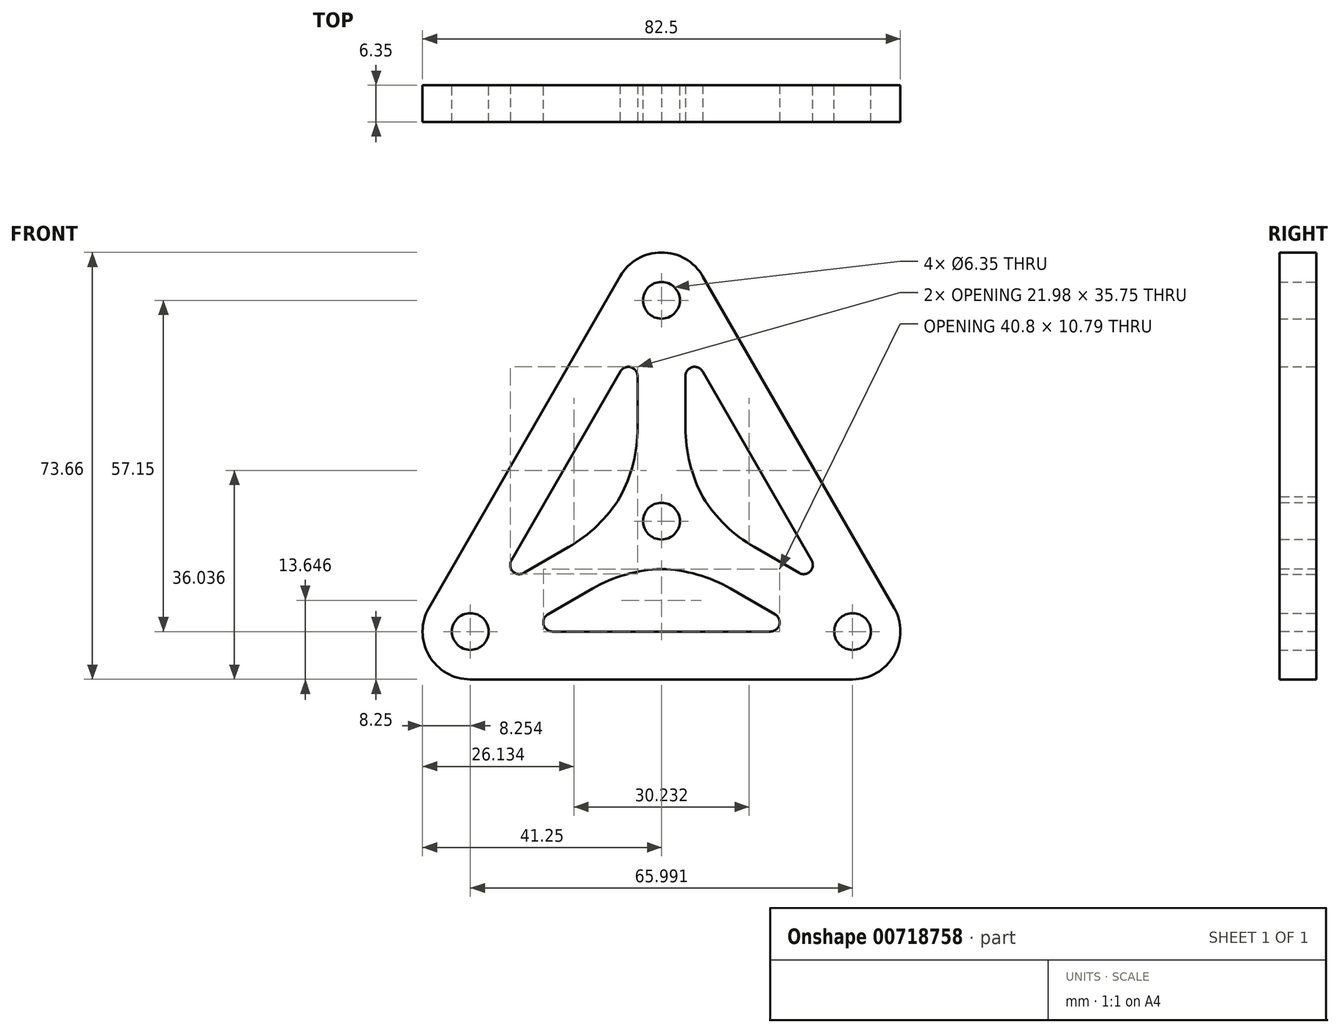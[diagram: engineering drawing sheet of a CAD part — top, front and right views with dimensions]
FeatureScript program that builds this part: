
annotation { "Feature Type Name" : "Feature", "Feature Type Description" : "" }
export const myFeature = defineFeature(function(context is Context, id is Id, definition is map)
    precondition{}
    {
        {
            var Q0;
            Q0=qCreatedBy(makeId("Front.planeOp"),FACE);
            var sketch = newSketch(context, id + "F0", { "sketchPlane" : qUnion([Q0])});
            skPoint(sketch, "E0", {"position": v(0, 38.1) * mm});
            skCircle(sketch, "E1", {"center": v(0, 38.1) * mm, "radius": 3.18 * mm});
            skCircle(sketch, "E2.1.0", {"center": v(-33, -19.05) * mm, "radius": 3.18 * mm});
            skPoint(sketch, "E2.1.1", {"position": v(-33, -19.05) * mm});
            skCircle(sketch, "E2.2.0", {"center": v(33, -19.05) * mm, "radius": 3.18 * mm});
            skPoint(sketch, "E2.2.1", {"position": v(33, -19.05) * mm});
            skPoint(sketch, "E2.center", {"position": v(0, 0) * mm});
            skLineSegment(sketch, "E3", {"start": v(-33, -19.05) * mm, "end": v(0, 38.1) * mm, "construction": true});
            skLineSegment(sketch, "E4", {"start": v(33, -19.05) * mm, "end": v(-33, -19.05) * mm, "construction": true});
            skLineSegment(sketch, "E5", {"start": v(33, -19.05) * mm, "end": v(0, 38.1) * mm, "construction": true});
            skLineSegment(sketch, "E6.0", {"start": v(40.14, -14.92) * mm, "end": v(7.15, 42.23) * mm});
            skLineSegment(sketch, "E6.1", {"start": v(33, -27.3) * mm, "end": v(-33, -27.3) * mm});
            skLineSegment(sketch, "E6.2", {"start": v(-40.14, -14.92) * mm, "end": v(-7.15, 42.23) * mm});
            skPoint(sketch, "E7.visualSharp", {"position": v(0, 54.61) * mm});
            skArc(sketch, "E7.filletArc", {"start": v(7.15, 42.23) * mm, "mid": v(0, 46.36) * mm, "end": v(-7.15, 42.23) * mm});
            skPoint(sketch, "E8.visualSharp", {"position": v(47.3, -27.3) * mm});
            skArc(sketch, "E8.filletArc", {"start": v(33, -27.3) * mm, "mid": v(40.14, -23.18) * mm, "end": v(40.14, -14.92) * mm});
            skPoint(sketch, "E9.visualSharp", {"position": v(-47.3, -27.3) * mm});
            skArc(sketch, "E9.filletArc", {"start": v(-40.14, -14.92) * mm, "mid": v(-40.14, -23.18) * mm, "end": v(-33, -27.3) * mm});
            skSolve(sketch);
        }
        {
            var Q0;
            Q0=qSketchRegion(id+"F0",true);
            extrude(context, id + "F1", {"entities" : qUnion([Q0]), "depth" : 6.35 * mm, "offsetDistance" : 25.4 * mm});
        }
        {
            var Q0;
            Q0=makeQuery(id+"F1.opExtrude","CAP_FACE",FACE,{"disambiguationData":[OSD([sQuery(id+"F0.wireOp",EDGE,"E1"),sQuery(id+"F0.wireOp",EDGE,"E2.1.0"),sQuery(id+"F0.wireOp",EDGE,"E2.2.0"),sQuery(id+"F0.wireOp",EDGE,"E6.0"),sQuery(id+"F0.wireOp",EDGE,"E6.1"),sQuery(id+"F0.wireOp",EDGE,"E6.2"),sQuery(id+"F0.wireOp",EDGE,"E7.filletArc"),sQuery(id+"F0.wireOp",EDGE,"E8.filletArc"),sQuery(id+"F0.wireOp",EDGE,"E9.filletArc")])],"isStart":false});
            var sketch = newSketch(context, id + "F2", { "sketchPlane" : qUnion([Q0])});
            skCircle(sketch, "E10", {"center": v(0, 0) * mm, "radius": 3.18 * mm});
            skSolve(sketch);
        }
        {
            var Q0;
            Q0 = qSketchRegion(id + "F2", true);
            extrude(context, id + "F3", {"entities" : qUnion([Q0]), "operationType" : NewBodyOperationType.REMOVE, "endBound" : BoundingType.THROUGH_ALL, "oppositeDirection" : true, "depth" : 25.4 * mm, "offsetDistance" : 25.4 * mm});
        }
        {
            var Q0;
            Q0=makeQuery(id+"F1.opExtrude","CAP_FACE",FACE,{"disambiguationData":[OSD([sQuery(id+"F0.wireOp",EDGE,"E1"),sQuery(id+"F0.wireOp",EDGE,"E2.1.0"),sQuery(id+"F0.wireOp",EDGE,"E2.2.0"),sQuery(id+"F0.wireOp",EDGE,"E6.0"),sQuery(id+"F0.wireOp",EDGE,"E6.1"),sQuery(id+"F0.wireOp",EDGE,"E6.2"),sQuery(id+"F0.wireOp",EDGE,"E7.filletArc"),sQuery(id+"F0.wireOp",EDGE,"E8.filletArc"),sQuery(id+"F0.wireOp",EDGE,"E9.filletArc")])],"isStart":false});
            var sketch = newSketch(context, id + "F4", { "sketchPlane" : qUnion([Q0])});
            skCircle(sketch, "E11", {"center": v(-33, -19.05) * mm, "radius": 8.25 * mm, "construction": true});
            skCircle(sketch, "E12", {"center": v(0, 38.1) * mm, "radius": 8.26 * mm, "construction": true});
            skCircle(sketch, "E13", {"center": v(33, -19.05) * mm, "radius": 8.26 * mm, "construction": true});
            skCircle(sketch, "E14", {"center": v(0, 0) * mm, "radius": 8.26 * mm});
            skLineSegment(sketch, "E15", {"start": v(-28.87, -11.9) * mm, "end": v(-4.13, 30.95) * mm});
            skLineSegment(sketch, "E16.1.0", {"start": v(24.74, -19.05) * mm, "end": v(-24.74, -19.05) * mm});
            skLineSegment(sketch, "E16.2.0", {"start": v(4.13, 30.95) * mm, "end": v(28.87, -11.9) * mm});
            skLineSegment(sketch, "E17", {"start": v(-4.13, 30.95) * mm, "end": v(-4.13, 7.15) * mm});
            skLineSegment(sketch, "E18", {"start": v(0, 38.1) * mm, "end": v(0, 41.28) * mm, "construction": true});
            skLineSegment(sketch, "E19.MirrorCS", {"start": v(4.13, 30.95) * mm, "end": v(4.13, 7.15) * mm});
            skLineSegment(sketch, "E20.1.0", {"start": v(-28.87, -11.9) * mm, "end": v(-8.25, 0) * mm});
            skLineSegment(sketch, "E20.1.1", {"start": v(-24.74, -19.05) * mm, "end": v(-4.13, -7.15) * mm});
            skLineSegment(sketch, "E20.2.0", {"start": v(24.74, -19.05) * mm, "end": v(4.13, -7.15) * mm});
            skLineSegment(sketch, "E20.2.1", {"start": v(28.87, -11.9) * mm, "end": v(8.26, 0) * mm});
            skLineSegment(sketch, "E21", {"start": v(-4.13, 30.95) * mm, "end": v(-4.13, 30.95) * mm});
            skLineSegment(sketch, "E22", {"start": v(4.13, 30.95) * mm, "end": v(4.13, 30.95) * mm});
            skLineSegment(sketch, "E23.1.0", {"start": v(-28.87, -11.9) * mm, "end": v(-28.87, -11.9) * mm});
            skLineSegment(sketch, "E23.1.1", {"start": v(-24.74, -19.05) * mm, "end": v(-24.74, -19.05) * mm});
            skLineSegment(sketch, "E23.2.0", {"start": v(24.74, -19.05) * mm, "end": v(24.74, -19.05) * mm});
            skLineSegment(sketch, "E23.2.1", {"start": v(28.87, -11.9) * mm, "end": v(28.87, -11.9) * mm});
            skSolve(sketch);
        }
        {
            var Q0;
            {var subQ0=sQuery(id+"F4.wireOp",EDGE,"E15");Q0=makeQuery(id+"F4.imprint","IMPRINT",FACE,{"disambiguationData":[TD([[makeQuery(id+"F4.imprint","IMPRINT",EDGE,{"derivedFrom":subQ0}),-1.0]])]});}
            var Q1;
            {var subQ0=sQuery(id+"F4.wireOp",EDGE,"E16.1.0");Q1=makeQuery(id+"F4.imprint","IMPRINT",FACE,{"disambiguationData":[TD([[makeQuery(id+"F4.imprint","IMPRINT",EDGE,{"derivedFrom":subQ0}),-1.0]])]});}
            var Q2;
            {var subQ0=sQuery(id+"F4.wireOp",EDGE,"E16.2.0");Q2=makeQuery(id+"F4.imprint","IMPRINT",FACE,{"disambiguationData":[TD([[makeQuery(id+"F4.imprint","IMPRINT",EDGE,{"derivedFrom":subQ0}),-1.0]])]});}
            extrude(context, id + "F5", {"entities" : qUnion([Q0, Q1, Q2]), "operationType" : NewBodyOperationType.REMOVE, "endBound" : BoundingType.THROUGH_ALL, "oppositeDirection" : true, "depth" : 25.4 * mm, "offsetDistance" : 25.4 * mm});
        }
        {
            var Q0;
            Q0=makeQuery(id+"F5.boolean.opBoolean","COPY",EDGE,{"derivedFrom":makeQuery(id+"F5.opExtrude","SWEPT_EDGE",EDGE,{"disambiguationData":[OSD([sQuery(id+"F4.wireOp",EDGE,"E14"),sQuery(id+"F4.wireOp",EDGE,"E17")])]})});
            var Q1;
            Q1=makeQuery(id+"F5.boolean.opBoolean","COPY",EDGE,{"derivedFrom":makeQuery(id+"F5.opExtrude","SWEPT_EDGE",EDGE,{"disambiguationData":[OSD([sQuery(id+"F4.wireOp",EDGE,"E14"),sQuery(id+"F4.wireOp",EDGE,"E20.1.0")])]})});
            var Q2;
            Q2=makeQuery(id+"F5.boolean.opBoolean","COPY",EDGE,{"derivedFrom":makeQuery(id+"F5.opExtrude","SWEPT_EDGE",EDGE,{"disambiguationData":[OSD([sQuery(id+"F4.wireOp",EDGE,"E14"),sQuery(id+"F4.wireOp",EDGE,"E20.1.1")])]})});
            var Q3;
            Q3=makeQuery(id+"F5.boolean.opBoolean","COPY",EDGE,{"derivedFrom":makeQuery(id+"F5.opExtrude","SWEPT_EDGE",EDGE,{"disambiguationData":[OSD([sQuery(id+"F4.wireOp",EDGE,"E14"),sQuery(id+"F4.wireOp",EDGE,"E20.2.0")])]})});
            var Q4;
            Q4=makeQuery(id+"F5.boolean.opBoolean","COPY",EDGE,{"derivedFrom":makeQuery(id+"F5.opExtrude","SWEPT_EDGE",EDGE,{"disambiguationData":[OSD([sQuery(id+"F4.wireOp",EDGE,"E14"),sQuery(id+"F4.wireOp",EDGE,"E20.2.1")])]})});
            var Q5;
            Q5=makeQuery(id+"F5.boolean.opBoolean","COPY",EDGE,{"derivedFrom":makeQuery(id+"F5.opExtrude","SWEPT_EDGE",EDGE,{"disambiguationData":[OSD([sQuery(id+"F4.wireOp",EDGE,"E14"),sQuery(id+"F4.wireOp",EDGE,"E19.MirrorCS")])]})});
            fillet(context, id + "F6", {"entities" : qUnion([Q0, Q1, Q2, Q3, Q4, Q5]), "radius" : 25.4 * mm, "tangentPropagation" : true, "allowEdgeOverflow" : false});
        }
        {
            var Q0;
            Q0=makeQuery(id+"F5.boolean.opBoolean","COPY",EDGE,{"derivedFrom":makeQuery(id+"F5.opExtrude","SWEPT_EDGE",EDGE,{"disambiguationData":[OSD([sQuery(id+"F4.wireOp",EDGE,"E16.2.0"),sQuery(id+"F4.wireOp",EDGE,"E19.MirrorCS")])]})});
            var Q1;
            Q1=makeQuery(id+"F5.boolean.opBoolean","COPY",EDGE,{"derivedFrom":makeQuery(id+"F5.opExtrude","SWEPT_EDGE",EDGE,{"disambiguationData":[OSD([sQuery(id+"F4.wireOp",EDGE,"E15"),sQuery(id+"F4.wireOp",EDGE,"E17")])]})});
            var Q2;
            Q2=makeQuery(id+"F5.boolean.opBoolean","COPY",EDGE,{"derivedFrom":makeQuery(id+"F5.opExtrude","SWEPT_EDGE",EDGE,{"disambiguationData":[OSD([sQuery(id+"F4.wireOp",EDGE,"E15"),sQuery(id+"F4.wireOp",EDGE,"E20.1.0")])]})});
            var Q3;
            Q3=makeQuery(id+"F5.boolean.opBoolean","COPY",EDGE,{"derivedFrom":makeQuery(id+"F5.opExtrude","SWEPT_EDGE",EDGE,{"disambiguationData":[OSD([sQuery(id+"F4.wireOp",EDGE,"E16.2.0"),sQuery(id+"F4.wireOp",EDGE,"E20.2.1")])]})});
            var Q4;
            Q4=makeQuery(id+"F5.boolean.opBoolean","COPY",EDGE,{"derivedFrom":makeQuery(id+"F5.opExtrude","SWEPT_EDGE",EDGE,{"disambiguationData":[OSD([sQuery(id+"F4.wireOp",EDGE,"E16.1.0"),sQuery(id+"F4.wireOp",EDGE,"E20.2.0")])]})});
            var Q5;
            Q5=makeQuery(id+"F5.boolean.opBoolean","COPY",EDGE,{"derivedFrom":makeQuery(id+"F5.opExtrude","SWEPT_EDGE",EDGE,{"disambiguationData":[OSD([sQuery(id+"F4.wireOp",EDGE,"E16.1.0"),sQuery(id+"F4.wireOp",EDGE,"E20.1.1")])]})});
            fillet(context, id + "F7", {"entities" : qUnion([Q0, Q1, Q2, Q3, Q4, Q5]), "radius" : 1.59 * mm, "tangentPropagation" : true, "allowEdgeOverflow" : false});
        }
    });
